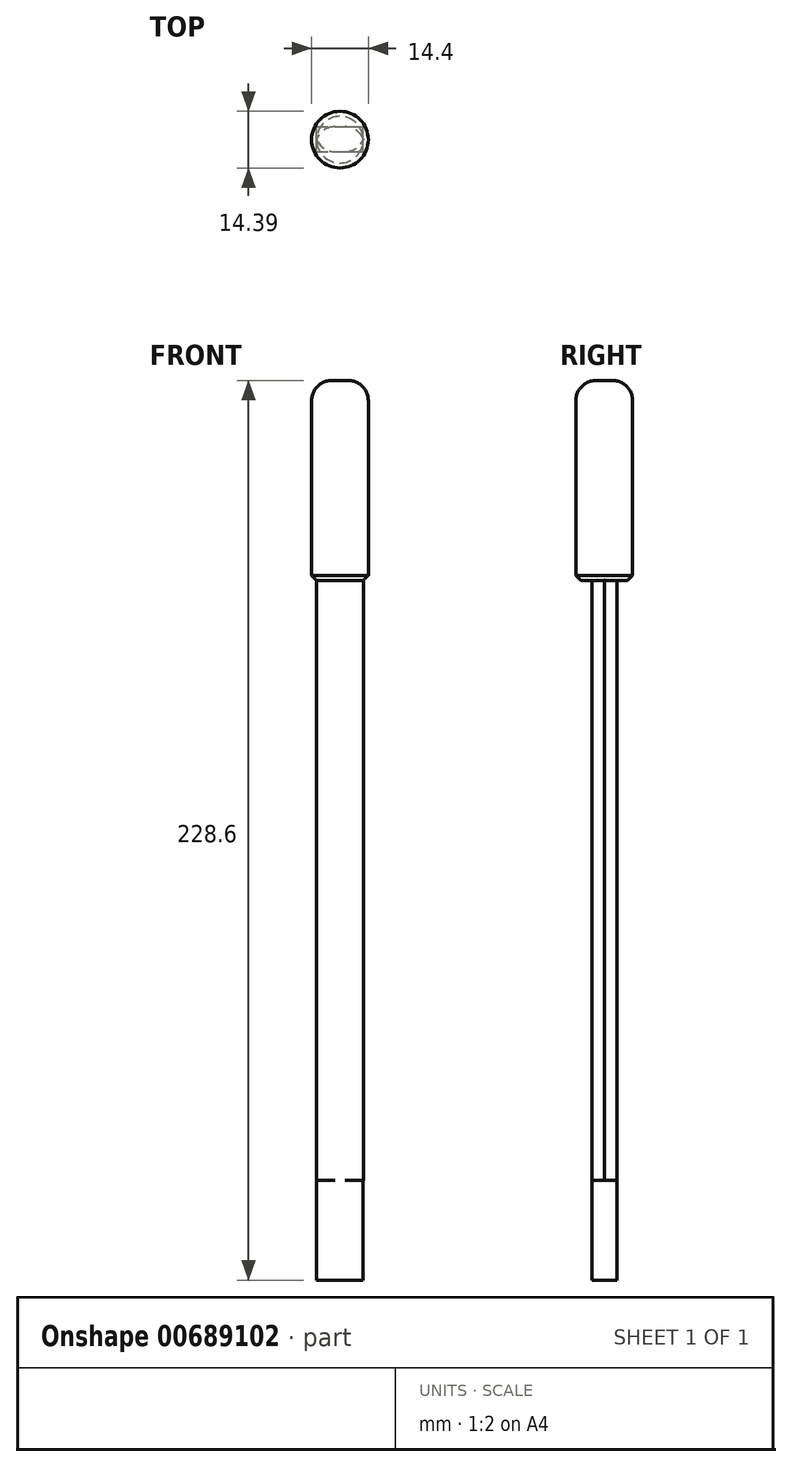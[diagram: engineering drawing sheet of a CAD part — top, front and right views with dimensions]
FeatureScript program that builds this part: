
annotation { "Feature Type Name" : "Feature", "Feature Type Description" : "" }
export const myFeature = defineFeature(function(context is Context, id is Id, definition is map)
    precondition{}
    {
        {
            var Q0;
            Q0=qCreatedBy(makeId("Front.planeOp"),FACE);
            var sketch = newSketch(context, id + "F0", { "sketchPlane" : qUnion([Q0])});
            skLineSegment(sketch, "E0.bottom", {"start": v(-6.35, 76.2) * mm, "end": v(6.35, 76.2) * mm});
            skLineSegment(sketch, "E0.top", {"start": v(-6.35, -76.2) * mm, "end": v(6.35, -76.2) * mm});
            skLineSegment(sketch, "E0.left", {"start": v(-6.35, 76.2) * mm, "end": v(-6.35, -76.2) * mm});
            skLineSegment(sketch, "E0.right", {"start": v(6.35, 76.2) * mm, "end": v(6.35, -76.2) * mm});
            skPoint(sketch, "E0.middle", {"position": v(0, 0) * mm});
            skSolve(sketch);
        }
        {
            var Q0;
            Q0 = qSketchRegion(id + "F0", true);
            extrude(context, id + "F1", {"entities" : qUnion([Q0]), "depth" : 6.35 * mm, "offsetDistance" : 25.4 * mm});
        }
        {
            var Q0;
            Q0=makeQuery(id+"F1.opExtrude","CAP_EDGE",EDGE,{"disambiguationData":[OSD([sQuery(id+"F0.wireOp",EDGE,"E0.right")])],"isStart":false});
            var Q1;
            Q1=makeQuery(id+"F1.opExtrude","CAP_EDGE",EDGE,{"disambiguationData":[OSD([sQuery(id+"F0.wireOp",EDGE,"E0.left")])],"isStart":false});
            var Q2;
            Q2=makeQuery(id+"F1.opExtrude","CAP_EDGE",EDGE,{"disambiguationData":[OSD([sQuery(id+"F0.wireOp",EDGE,"E0.left")])],"isStart":true});
            var Q3;
            Q3=makeQuery(id+"F1.opExtrude","CAP_EDGE",EDGE,{"disambiguationData":[OSD([sQuery(id+"F0.wireOp",EDGE,"E0.right")])],"isStart":true});
            fillet(context, id + "F2", {"entities" : qUnion([Q0, Q1, Q2, Q3]), "radius" : 5.08 * mm, "tangentPropagation" : true, "allowEdgeOverflow" : false});
        }
        {
            var Q0;
            Q0=makeQuery(id+"F1.opExtrude","SWEPT_FACE",FACE,{"disambiguationData":[OSD([sQuery(id+"F0.wireOp",EDGE,"E0.top")])]});
            var sketch = newSketch(context, id + "F3", { "sketchPlane" : qUnion([Q0])});
            skLineSegment(sketch, "E1.bottom", {"start": v(-5.98, 6.35) * mm, "end": v(5.9, 6.35) * mm});
            skLineSegment(sketch, "E1.top", {"start": v(-5.98, 0) * mm, "end": v(5.9, 0) * mm});
            skLineSegment(sketch, "E1.left", {"start": v(-5.98, 6.35) * mm, "end": v(-5.98, 0) * mm});
            skLineSegment(sketch, "E1.right", {"start": v(5.9, 6.35) * mm, "end": v(5.9, 0) * mm});
            skSolve(sketch);
        }
        {
            var Q0;
            Q0 = qSketchRegion(id + "F3", true);
            extrude(context, id + "F4", {"entities" : qUnion([Q0]), "operationType" : NewBodyOperationType.ADD, "depth" : 25.4 * mm, "offsetDistance" : 25.4 * mm});
        }
        {
            var Q0;
            Q0=makeQuery(id+"F1.opExtrude","SWEPT_FACE",FACE,{"disambiguationData":[OSD([sQuery(id+"F0.wireOp",EDGE,"E0.bottom")])]});
            var sketch = newSketch(context, id + "F5", { "sketchPlane" : qUnion([Q0])});
            skSolve(sketch);
        }
        {
            var Q0;
            {var subQ0=sQuery(id+"F0.wireOp",EDGE,"E0.bottom");Q0=makeQuery(id+"F5.imprint","IMPRINT",FACE,{"disambiguationData":[TD([[makeQuery(id+"F5.imprint","IMPRINT",EDGE,{"derivedFrom":makeQuery(id+"F1.opExtrude","CAP_EDGE",EDGE,{"disambiguationData":[OSD([subQ0])],"isStart":true})}),-1.0]])]});}
            var sketch = newSketch(context, id + "F6", { "sketchPlane" : qUnion([Q0])});
            skCircle(sketch, "E2", {"center": v(0, -3.28) * mm, "radius": 7.2 * mm});
            skSolve(sketch);
        }
        {
            var Q0;
            Q0 = qSketchRegion(id + "F6", true);
            extrude(context, id + "F7", {"entities" : qUnion([Q0]), "operationType" : NewBodyOperationType.ADD, "depth" : 50.8 * mm, "offsetDistance" : 25.4 * mm});
        }
        {
            var Q0;
            Q0=makeQuery(id+"F7.opExtrude","CAP_EDGE",EDGE,{"disambiguationData":[OSD([sQuery(id+"F6.wireOp",EDGE,"E2")])],"isStart":false});
            fillet(context, id + "F8", {"entities" : qUnion([Q0]), "radius" : 5.08 * mm, "tangentPropagation" : true, "allowEdgeOverflow" : false});
        }
        {
            var Q0;
            Q0=makeQuery(id+"F7.opExtrude","CAP_EDGE",EDGE,{"disambiguationData":[OSD([sQuery(id+"F6.wireOp",EDGE,"E2")])],"isStart":true});
            chamfer(context, id + "F9", {"entities" : qUnion([Q0]), "width" : 1.27 * mm, "tangentPropagation" : true});
        }
    });
